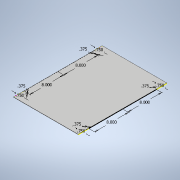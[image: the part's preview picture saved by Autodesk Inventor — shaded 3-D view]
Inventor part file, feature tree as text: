
AUTODESK INVENTOR PART (.ipt)
format: ipt  version: 2021 (Build 250183000, 183)  size: 150,016 bytes
history: native  units: in
note: dims shown in document units (in); Inventor stores cm internally (conversion verified against a paired STEP export)
features: extrude x2, sketch x2, hole x1
ambient origin geometry x8: Origin, YZ Plane, XZ Plane, XY Plane, X Axis, Y Axis, Z Axis, Center Point
bodies: Solid1 (feature_tree)
feature tree (5):
  extrude  "Extrusion1"  Depth=10.5in
  sketch  "Sketch2"  dims[d14=10.5in d15=10.5in d16=10.5in d17=0.06in d18=0.0in d19=6.5in d20=1.25in d21=5.1in d22=1.25in d23=1.25in d24=1.25in d25=6.5in d26=5.1in d27=1.25in d28=1.25in d29=8.0in d30=0.75in d31=0.375in d32=8.0in d33=0.75in d34=0.375in d35=8.0in d36=0.75in d37=8.0in d38=0.75in d39=0.375in d40=0.375in d41=1.0in d42=0.0in d43=0.201in d44=0.75in d45=0.385in d46=0.25in d47=0.5635in d48=1.0in d49=0.8108in]
  extrude  "Extrusion2"  Depth=10.5in
  hole  "Hole1"  [1 undecoded]
  sketch  "Sketch1"  dims[d12=15.28in d13=10.5in]
note: 1 required parameter value undecoded (feature->parameter linkage not recoverable at this tier; creation-order binding heuristic only, values carry confidence <= 0.55)
